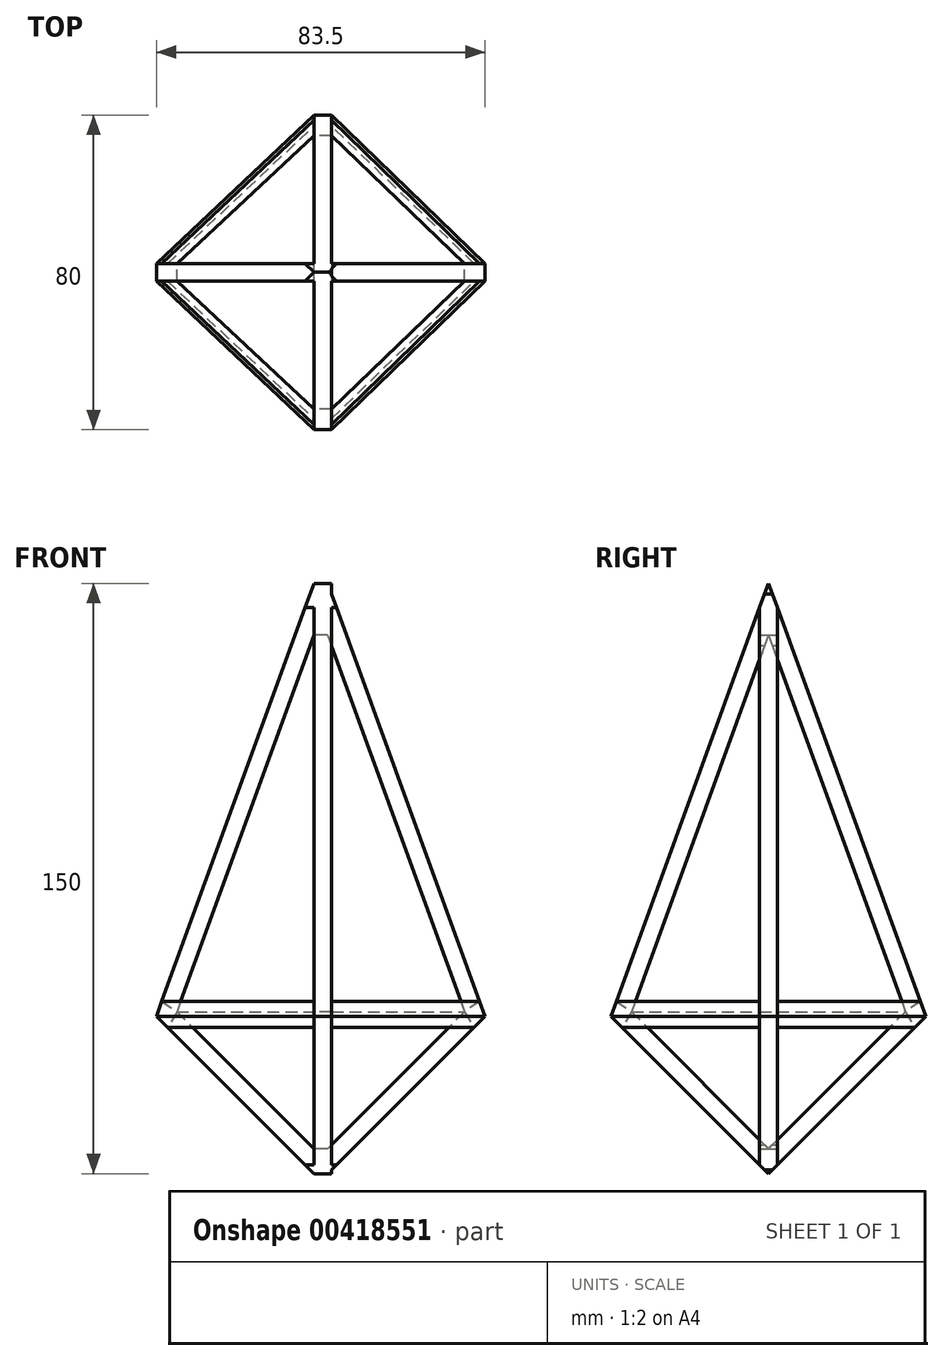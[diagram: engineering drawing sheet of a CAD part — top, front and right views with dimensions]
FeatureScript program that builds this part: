
annotation { "Feature Type Name" : "Feature", "Feature Type Description" : "" }
export const myFeature = defineFeature(function(context is Context, id is Id, definition is map)
    precondition{}
    {
        {
            var Q0;
            Q0=qCreatedBy(makeId("Right.planeOp"),FACE);
            var sketch = newSketch(context, id + "F0", { "sketchPlane" : qUnion([Q0])});
            skLineSegment(sketch, "E0", {"start": v(0, 0) * mm, "end": v(40, 40) * mm});
            skLineSegment(sketch, "E1", {"start": v(40, 40) * mm, "end": v(0, 150) * mm});
            skLineSegment(sketch, "E2", {"start": v(0, 136.83) * mm, "end": v(34.8, 41.16) * mm});
            skLineSegment(sketch, "E3", {"start": v(34.8, 41.16) * mm, "end": v(0, 6.36) * mm});
            skLineSegment(sketch, "E4", {"start": v(0, 168.02) * mm, "end": v(0, -17.8) * mm, "construction": true});
            skLineSegment(sketch, "E5.MirrorCS", {"start": v(-40, 40) * mm, "end": v(0, 150) * mm});
            skLineSegment(sketch, "E6.MirrorCS", {"start": v(-34.8, 41.16) * mm, "end": v(0, 6.36) * mm});
            skLineSegment(sketch, "E7.MirrorCS", {"start": v(0, 0) * mm, "end": v(-40, 40) * mm});
            skLineSegment(sketch, "E8.MirrorCS", {"start": v(0, 136.83) * mm, "end": v(-34.8, 41.16) * mm});
            skSolve(sketch);
        }
        {
            var Q0;
            Q0 = qSketchRegion(id + "F0", true);
            extrude(context, id + "F1", {"entities" : qUnion([Q0]), "depth" : 4.5 * mm});
        }
        {
            var Q0;
            Q0=qCreatedBy(makeId("Right.planeOp"),FACE);
            cPlane(context, id + "F2", {"entities" : qUnion([Q0]), "cplaneType" : CPlaneType.OFFSET, "offset" : (3.5 / 2) * mm, "width" : 150 * mm, "height" : 150 * mm});
        }
        {
            var Q0;
            Q0=qCreatedBy(id+"F2.planeOp",FACE);
            var sketch = newSketch(context, id + "F3", { "sketchPlane" : qUnion([Q0])});
            skLineSegment(sketch, "E9", {"start": v(0, 157.89) * mm, "end": v(0, -32.93) * mm, "construction": true});
            skSolve(sketch);
        }
        {
            var Q0;
            Q0=qCreatedBy(makeId("Front.planeOp"),FACE);
            var sketch = newSketch(context, id + "F4", { "sketchPlane" : qUnion([Q0])});
            skLineSegment(sketch, "E10", {"start": v(0, 0) * mm, "end": v(-40, 40) * mm});
            skLineSegment(sketch, "E11", {"start": v(-40, 40) * mm, "end": v(0, 150) * mm});
            skLineSegment(sketch, "E12", {"start": v(0, 150) * mm, "end": v(0, 136.83) * mm});
            skLineSegment(sketch, "E13", {"start": v(0, 136.83) * mm, "end": v(-34.8, 41.16) * mm});
            skLineSegment(sketch, "E14", {"start": v(-34.8, 41.16) * mm, "end": v(0, 6.36) * mm});
            skLineSegment(sketch, "E15", {"start": v(0, 6.36) * mm, "end": v(0, 0) * mm});
            skLineSegment(sketch, "E16.MirrorCS", {"start": v(3.5, 6.36) * mm, "end": v(3.5, 0) * mm});
            skLineSegment(sketch, "E17.MirrorCS", {"start": v(3.5, 150) * mm, "end": v(3.5, 136.83) * mm});
            skLineSegment(sketch, "E18.MirrorCS", {"start": v(43.5, 40) * mm, "end": v(3.5, 150) * mm});
            skLineSegment(sketch, "E19.MirrorCS", {"start": v(38.3, 41.16) * mm, "end": v(3.5, 6.36) * mm});
            skLineSegment(sketch, "E20.MirrorCS", {"start": v(3.5, 0) * mm, "end": v(43.5, 40) * mm});
            skLineSegment(sketch, "E21.MirrorCS", {"start": v(3.5, 136.83) * mm, "end": v(38.3, 41.16) * mm});
            skSolve(sketch);
        }
        {
            var Q0;
            Q0 = qSketchRegion(id + "F4", true);
            extrude(context, id + "F5", {"entities" : qUnion([Q0]), "operationType" : NewBodyOperationType.ADD, "endBound" : BoundingType.SYMMETRIC, "depth" : 4.5 * mm});
        }
        {
            var Q0;
            Q0=qCreatedBy(id+"F2.planeOp",FACE);
            var sketch = newSketch(context, id + "F6", { "sketchPlane" : qUnion([Q0])});
            skLineSegment(sketch, "E22", {"start": v(-40, 40) * mm, "end": v(0, 150) * mm});
            skLineSegment(sketch, "E23", {"start": v(0, 150) * mm, "end": v(-46.87, 150) * mm});
            skLineSegment(sketch, "E24", {"start": v(-46.87, 150) * mm, "end": v(-40, 40) * mm});
            skLineSegment(sketch, "E25.MirrorCS", {"start": v(0, 150) * mm, "end": v(46.87, 150) * mm});
            skLineSegment(sketch, "E26.MirrorCS", {"start": v(40, 40) * mm, "end": v(0, 150) * mm});
            skLineSegment(sketch, "E27.MirrorCS", {"start": v(46.87, 150) * mm, "end": v(40, 40) * mm});
            skLineSegment(sketch, "E28", {"start": v(-40, 40) * mm, "end": v(0, 0) * mm});
            skLineSegment(sketch, "E29", {"start": v(0, 0) * mm, "end": v(40, 40) * mm});
            skLineSegment(sketch, "E30", {"start": v(40, 40) * mm, "end": v(40, 0) * mm});
            skLineSegment(sketch, "E31", {"start": v(40, 0) * mm, "end": v(0, 0) * mm});
            skLineSegment(sketch, "E32", {"start": v(-40, 40) * mm, "end": v(-40, 0) * mm});
            skLineSegment(sketch, "E33", {"start": v(-40, 0) * mm, "end": v(0, 0) * mm});
            skSolve(sketch);
        }
        {
            var Q0;
            Q0=makeQuery(id+"F6.imprint","IMPRINT",FACE,{"disambiguationData":[TD([[makeQuery(id+"F6.imprint","IMPRINT",EDGE,{"derivedFrom":sQuery(id+"F6.wireOp",EDGE,"E22")}),1.0]])]});
            var Q1;
            Q1=makeQuery(id+"F6.imprint","IMPRINT",FACE,{"disambiguationData":[TD([[makeQuery(id+"F6.imprint","IMPRINT",EDGE,{"derivedFrom":sQuery(id+"F6.wireOp",EDGE,"E25.MirrorCS")}),-1.0]])]});
            var Q2;
            Q2=makeQuery(id+"F6.imprint","IMPRINT",FACE,{"disambiguationData":[TD([[makeQuery(id+"F6.imprint","IMPRINT",EDGE,{"derivedFrom":sQuery(id+"F6.wireOp",EDGE,"E28")}),-1.0]])]});
            var Q3;
            Q3=makeQuery(id+"F6.imprint","IMPRINT",FACE,{"disambiguationData":[TD([[makeQuery(id+"F6.imprint","IMPRINT",EDGE,{"derivedFrom":sQuery(id+"F6.wireOp",EDGE,"E29")}),-1.0]])]});
            extrude(context, id + "F7", {"entities" : qUnion([Q0, Q1, Q2, Q3]), "operationType" : NewBodyOperationType.REMOVE, "endBound" : BoundingType.SYMMETRIC, "oppositeDirection" : true, "depth" : 25 * mm});
        }
        {
            var Q0;
            {var subQ0=sQuery(id+"F0.wireOp",EDGE,"E8.MirrorCS");var subQ1=sQuery(id+"F0.wireOp",EDGE,"E7.MirrorCS");var subQ4=sQuery(id+"F0.wireOp",EDGE,"E6.MirrorCS");var subQ5=sQuery(id+"F0.wireOp",EDGE,"E5.MirrorCS");Q0=makeQuery(id+"F5.boolean.opBoolean","SPLIT",FACE,{"disambiguationData":[TD([makeQuery(id+"F1.opExtrude","SWEPT_FACE",FACE,{"disambiguationData":[OSD([subQ4])]})])],"derivedFrom":makeQuery(id+"F1.opExtrude","CAP_FACE",FACE,{"disambiguationData":[OSD([sQuery(id+"F0.wireOp",EDGE,"E0"),sQuery(id+"F0.wireOp",EDGE,"E1"),sQuery(id+"F0.wireOp",EDGE,"E2"),sQuery(id+"F0.wireOp",EDGE,"E3"),subQ5,subQ4,subQ1,subQ0])],"isStart":false})});}
            var sketch = newSketch(context, id + "F8", { "sketchPlane" : qUnion([Q0])});
            skLineSegment(sketch, "E34", {"start": v(-40, 40) * mm, "end": v(-38.63, 43.76) * mm});
            skLineSegment(sketch, "E35", {"start": v(-38.63, 43.76) * mm, "end": v(-34.8, 41.16) * mm});
            skLineSegment(sketch, "E36", {"start": v(-34.8, 41.16) * mm, "end": v(-37.17, 37.17) * mm});
            skLineSegment(sketch, "E37", {"start": v(-37.17, 37.17) * mm, "end": v(-40, 40) * mm});
            skSolve(sketch);
        }
        {
            var Q0;
            Q0=makeQuery(id+"F5.opExtrude","CAP_FACE",FACE,{"disambiguationData":[OSD([sQuery(id+"F4.wireOp",EDGE,"E16.MirrorCS"),sQuery(id+"F4.wireOp",EDGE,"E17.MirrorCS"),sQuery(id+"F4.wireOp",EDGE,"E18.MirrorCS"),sQuery(id+"F4.wireOp",EDGE,"E19.MirrorCS"),sQuery(id+"F4.wireOp",EDGE,"E20.MirrorCS"),sQuery(id+"F4.wireOp",EDGE,"E21.MirrorCS")])],"isStart":false});
            var sketch = newSketch(context, id + "F9", { "sketchPlane" : qUnion([Q0])});
            skLineSegment(sketch, "E38", {"start": v(43.5, 40) * mm, "end": v(42.13, 43.76) * mm});
            skLineSegment(sketch, "E39", {"start": v(42.13, 43.76) * mm, "end": v(38.3, 41.16) * mm});
            skLineSegment(sketch, "E40", {"start": v(38.3, 41.16) * mm, "end": v(40.67, 37.17) * mm});
            skLineSegment(sketch, "E41", {"start": v(40.67, 37.17) * mm, "end": v(43.5, 40) * mm});
            skSolve(sketch);
        }
        {
            var Q1;
            Q1 = qSketchRegion(id + "F8", true);
            var Q2;
            Q2 = qSketchRegion(id + "F9", true);
            loft(context, id + "F10", {"operationType" : NewBodyOperationType.ADD, "sheetProfilesArray" : [{ "sheetProfileEntities" : qUnion([Q1]) }, { "sheetProfileEntities" : qUnion([Q2]) }]});
        }
        {
            var Q0;
            Q0=makeQuery(id+"F5.opExtrude","CAP_FACE",FACE,{"disambiguationData":[OSD([sQuery(id+"F4.wireOp",EDGE,"E16.MirrorCS"),sQuery(id+"F4.wireOp",EDGE,"E17.MirrorCS"),sQuery(id+"F4.wireOp",EDGE,"E18.MirrorCS"),sQuery(id+"F4.wireOp",EDGE,"E19.MirrorCS"),sQuery(id+"F4.wireOp",EDGE,"E20.MirrorCS"),sQuery(id+"F4.wireOp",EDGE,"E21.MirrorCS")])],"isStart":true});
            var sketch = newSketch(context, id + "F11", { "sketchPlane" : qUnion([Q0])});
            skLineSegment(sketch, "E42", {"start": v(-43.5, 40) * mm, "end": v(-42.13, 43.76) * mm});
            skLineSegment(sketch, "E43", {"start": v(-42.13, 43.76) * mm, "end": v(-38.3, 41.16) * mm});
            skLineSegment(sketch, "E44", {"start": v(-38.3, 41.16) * mm, "end": v(-40.67, 37.17) * mm});
            skLineSegment(sketch, "E45", {"start": v(-40.67, 37.17) * mm, "end": v(-43.5, 40) * mm});
            skSolve(sketch);
        }
        {
            var Q0;
            {var subQ0=sQuery(id+"F0.wireOp",EDGE,"E2");var subQ1=sQuery(id+"F0.wireOp",EDGE,"E1");var subQ2=sQuery(id+"F0.wireOp",EDGE,"E3");var subQ3=sQuery(id+"F0.wireOp",EDGE,"E0");Q0=makeQuery(id+"F5.boolean.opBoolean","SPLIT",FACE,{"disambiguationData":[TD([makeQuery(id+"F1.opExtrude","SWEPT_FACE",FACE,{"disambiguationData":[OSD([subQ0])]})])],"derivedFrom":makeQuery(id+"F1.opExtrude","CAP_FACE",FACE,{"disambiguationData":[OSD([subQ3,subQ1,subQ0,subQ2,sQuery(id+"F0.wireOp",EDGE,"E5.MirrorCS"),sQuery(id+"F0.wireOp",EDGE,"E6.MirrorCS"),sQuery(id+"F0.wireOp",EDGE,"E7.MirrorCS"),sQuery(id+"F0.wireOp",EDGE,"E8.MirrorCS")])],"isStart":false})});}
            var sketch = newSketch(context, id + "F12", { "sketchPlane" : qUnion([Q0])});
            skLineSegment(sketch, "E46", {"start": v(40, 40) * mm, "end": v(38.63, 43.76) * mm});
            skLineSegment(sketch, "E47", {"start": v(38.63, 43.76) * mm, "end": v(34.8, 41.16) * mm});
            skLineSegment(sketch, "E48", {"start": v(34.8, 41.16) * mm, "end": v(37.17, 37.17) * mm});
            skLineSegment(sketch, "E49", {"start": v(37.17, 37.17) * mm, "end": v(40, 40) * mm});
            skSolve(sketch);
        }
        {
            var Q1;
            Q1 = qSketchRegion(id + "F11", true);
            var Q2;
            Q2 = qSketchRegion(id + "F12", true);
            loft(context, id + "F13", {"operationType" : NewBodyOperationType.ADD, "sheetProfilesArray" : [{ "sheetProfileEntities" : qUnion([Q1]) }, { "sheetProfileEntities" : qUnion([Q2]) }]});
        }
        {
            var Q0;
            {var subQ1=sQuery(id+"F0.wireOp",EDGE,"E1");var subQ5=sQuery(id+"F0.wireOp",EDGE,"E0");var subQ6=sQuery(id+"F0.wireOp",EDGE,"E8.MirrorCS");var subQ7=sQuery(id+"F0.wireOp",EDGE,"E6.MirrorCS");var subQ8=sQuery(id+"F0.wireOp",EDGE,"E3");var subQ9=sQuery(id+"F0.wireOp",EDGE,"E2");var subQ10=makeQuery(id+"F1.opExtrude","CAP_FACE",FACE,{"disambiguationData":[OSD([subQ5,subQ1,subQ9,subQ8,sQuery(id+"F0.wireOp",EDGE,"E5.MirrorCS"),subQ7,sQuery(id+"F0.wireOp",EDGE,"E7.MirrorCS"),subQ6])],"isStart":true});Q0=makeQuery(id+"F5.boolean.opBoolean","SPLIT",FACE,{"disambiguationData":[TD([makeQuery(id+"F1.opExtrude","SWEPT_FACE",FACE,{"disambiguationData":[OSD([subQ5])]})])],"derivedFrom":subQ10});}
            var sketch = newSketch(context, id + "F14", { "sketchPlane" : qUnion([Q0])});
            skLineSegment(sketch, "E50", {"start": v(-40, 40) * mm, "end": v(-38.63, 43.76) * mm});
            skLineSegment(sketch, "E51", {"start": v(-38.63, 43.76) * mm, "end": v(-34.8, 41.16) * mm});
            skLineSegment(sketch, "E52", {"start": v(-34.8, 41.16) * mm, "end": v(-37.17, 37.17) * mm});
            skLineSegment(sketch, "E53", {"start": v(-37.17, 37.17) * mm, "end": v(-40, 40) * mm});
            skSolve(sketch);
        }
        {
            var Q0;
            Q0=makeQuery(id+"F5.opExtrude","CAP_FACE",FACE,{"disambiguationData":[OSD([sQuery(id+"F4.wireOp",EDGE,"E10"),sQuery(id+"F4.wireOp",EDGE,"E11"),sQuery(id+"F4.wireOp",EDGE,"E12"),sQuery(id+"F4.wireOp",EDGE,"E13"),sQuery(id+"F4.wireOp",EDGE,"E14"),sQuery(id+"F4.wireOp",EDGE,"E15")])],"isStart":true});
            var sketch = newSketch(context, id + "F15", { "sketchPlane" : qUnion([Q0])});
            skLineSegment(sketch, "E54", {"start": v(40, 40) * mm, "end": v(38.63, 43.76) * mm});
            skLineSegment(sketch, "E55", {"start": v(38.63, 43.76) * mm, "end": v(34.8, 41.16) * mm});
            skLineSegment(sketch, "E56", {"start": v(34.8, 41.16) * mm, "end": v(37.17, 37.17) * mm});
            skLineSegment(sketch, "E57", {"start": v(37.17, 37.17) * mm, "end": v(40, 40) * mm});
            skSolve(sketch);
        }
        {
            var Q1;
            Q1 = qSketchRegion(id + "F15", true);
            var Q2;
            Q2 = qSketchRegion(id + "F14", true);
            loft(context, id + "F16", {"operationType" : NewBodyOperationType.ADD, "sheetProfilesArray" : [{ "sheetProfileEntities" : qUnion([Q1]) }, { "sheetProfileEntities" : qUnion([Q2]) }]});
        }
        {
            var Q0;
            Q0=makeQuery(id+"F5.opExtrude","CAP_FACE",FACE,{"disambiguationData":[OSD([sQuery(id+"F4.wireOp",EDGE,"E10"),sQuery(id+"F4.wireOp",EDGE,"E11"),sQuery(id+"F4.wireOp",EDGE,"E12"),sQuery(id+"F4.wireOp",EDGE,"E13"),sQuery(id+"F4.wireOp",EDGE,"E14"),sQuery(id+"F4.wireOp",EDGE,"E15")])],"isStart":false});
            var sketch = newSketch(context, id + "F17", { "sketchPlane" : qUnion([Q0])});
            skLineSegment(sketch, "E58", {"start": v(-40, 40) * mm, "end": v(-38.63, 43.76) * mm});
            skLineSegment(sketch, "E59", {"start": v(-38.63, 43.76) * mm, "end": v(-34.8, 41.16) * mm});
            skLineSegment(sketch, "E60", {"start": v(-34.8, 41.16) * mm, "end": v(-37.17, 37.17) * mm});
            skLineSegment(sketch, "E61", {"start": v(-37.17, 37.17) * mm, "end": v(-40, 40) * mm});
            skSolve(sketch);
        }
        {
            var Q0;
            {var subQ1=sQuery(id+"F0.wireOp",EDGE,"E2");var subQ5=sQuery(id+"F0.wireOp",EDGE,"E8.MirrorCS");var subQ6=sQuery(id+"F0.wireOp",EDGE,"E7.MirrorCS");var subQ7=sQuery(id+"F0.wireOp",EDGE,"E6.MirrorCS");var subQ8=sQuery(id+"F0.wireOp",EDGE,"E5.MirrorCS");var subQ9=sQuery(id+"F0.wireOp",EDGE,"E3");var subQ10=makeQuery(id+"F1.opExtrude","CAP_FACE",FACE,{"disambiguationData":[OSD([sQuery(id+"F0.wireOp",EDGE,"E0"),sQuery(id+"F0.wireOp",EDGE,"E1"),subQ1,subQ9,subQ8,subQ7,subQ6,subQ5])],"isStart":true});Q0=makeQuery(id+"F5.boolean.opBoolean","SPLIT",FACE,{"disambiguationData":[TD([makeQuery(id+"F1.opExtrude","SWEPT_FACE",FACE,{"disambiguationData":[OSD([subQ8])]})])],"derivedFrom":subQ10});}
            var sketch = newSketch(context, id + "F18", { "sketchPlane" : qUnion([Q0])});
            skLineSegment(sketch, "E62", {"start": v(40, 40) * mm, "end": v(38.63, 43.76) * mm});
            skLineSegment(sketch, "E63", {"start": v(38.63, 43.76) * mm, "end": v(34.8, 41.16) * mm});
            skLineSegment(sketch, "E64", {"start": v(34.8, 41.16) * mm, "end": v(37.17, 37.17) * mm});
            skLineSegment(sketch, "E65", {"start": v(37.17, 37.17) * mm, "end": v(40, 40) * mm});
            skSolve(sketch);
        }
        {
            var Q1;
            Q1 = qSketchRegion(id + "F17", true);
            var Q2;
            Q2 = qSketchRegion(id + "F18", true);
            loft(context, id + "F19", {"operationType" : NewBodyOperationType.ADD, "sheetProfilesArray" : [{ "sheetProfileEntities" : qUnion([Q1]) }, { "sheetProfileEntities" : qUnion([Q2]) }]});
        }
    });
